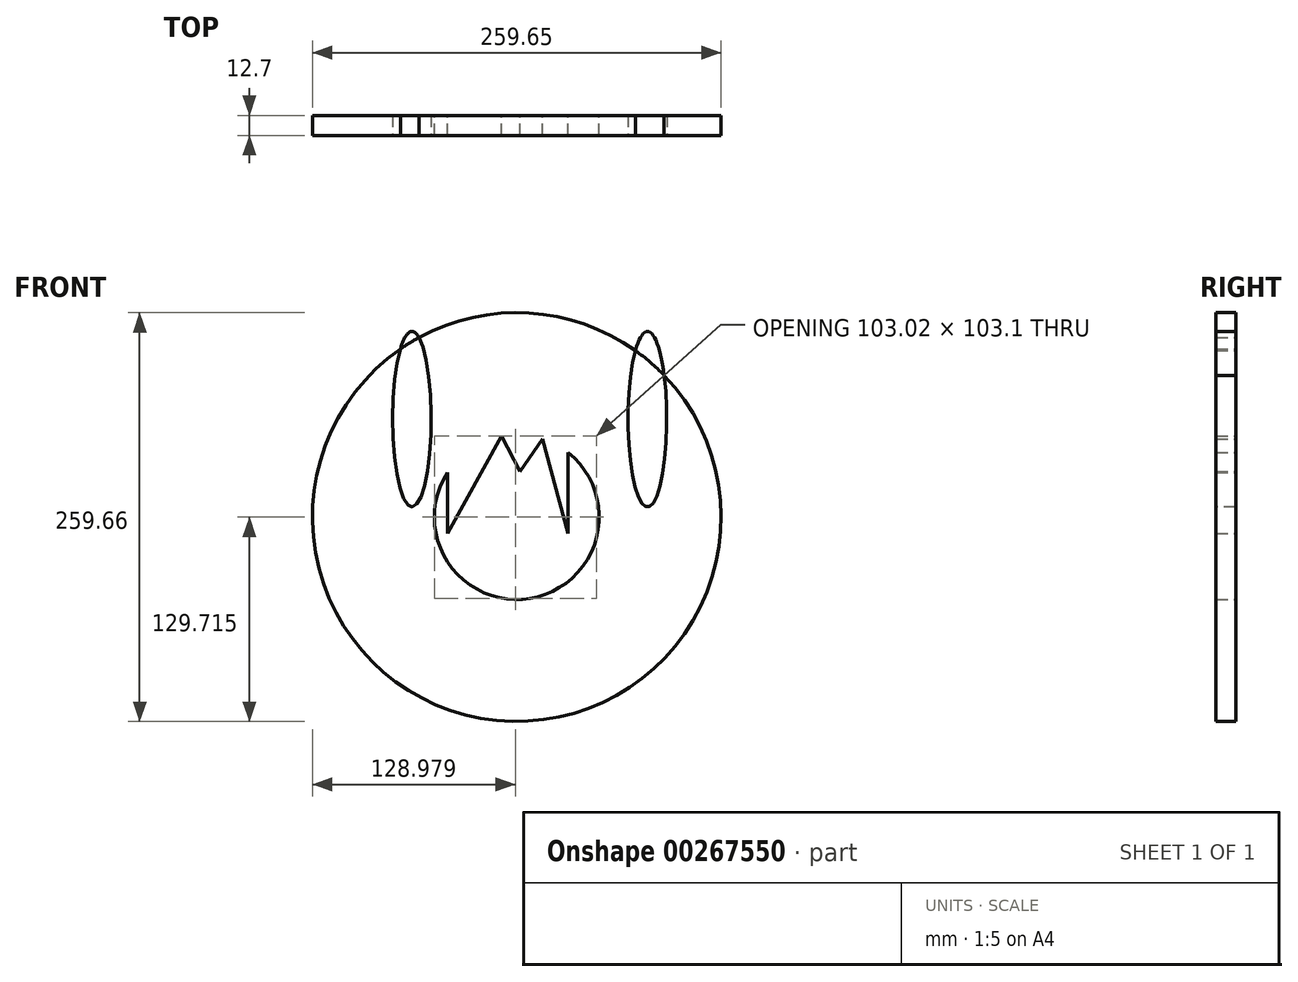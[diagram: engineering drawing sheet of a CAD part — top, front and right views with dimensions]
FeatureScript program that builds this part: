
annotation { "Feature Type Name" : "Feature", "Feature Type Description" : "" }
export const myFeature = defineFeature(function(context is Context, id is Id, definition is map)
    precondition{}
    {
        {
            var Q0;
            Q0=qCreatedBy(makeId("Front.planeOp"),FACE);
            var sketch = newSketch(context, id + "F0", { "sketchPlane" : qUnion([Q0])});
            skCircle(sketch, "E0", {"center": v(-217.67, 116.96) * mm, "radius": 129.83 * mm});
            skEllipse(sketch, "E1", {"center": v(-284.27, 179.1) * mm, "majorRadius": 55.69 * mm, "minorRadius": 12.28 * mm, "majorAxis": v(0, -1)});
            skEllipse(sketch, "E2.MirrorC", {"center": v(-134.69, 179.1) * mm, "majorRadius": 55.69 * mm, "minorRadius": 12.28 * mm, "majorAxis": v(0, -1)});
            skArc(sketch, "E3.0", {"start": v(-261.7, 145.3) * mm, "mid": v(-209.18, 65.3) * mm, "end": v(-185.04, 157.9) * mm});
            skLineSegment(sketch, "E4", {"start": v(-261.7, 145.3) * mm, "end": v(-261.7, 106.38) * mm});
            skLineSegment(sketch, "E5", {"start": v(-261.7, 106.38) * mm, "end": v(-227.46, 168.4) * mm});
            skLineSegment(sketch, "E6", {"start": v(-227.46, 168.4) * mm, "end": v(-215.76, 145.85) * mm});
            skLineSegment(sketch, "E7", {"start": v(-215.76, 145.85) * mm, "end": v(-201.2, 166.65) * mm});
            skLineSegment(sketch, "E8", {"start": v(-201.2, 166.65) * mm, "end": v(-185.04, 106.38) * mm});
            skLineSegment(sketch, "E9", {"start": v(-185.04, 106.38) * mm, "end": v(-185.04, 157.9) * mm});
            skSolve(sketch);
        }
        {
            var Q0;
            {var subQ0=sQuery(id+"F0.wireOp",EDGE,"E2.MirrorC");var subQ1=sQuery(id+"F0.wireOp",EDGE,"E0");var subQ2=makeQuery(id+"F0.imprint","INTERSECT",VERTEX,{"disambiguationData":[OD(0.0)],"derivedFrom":[subQ1,subQ0]});Q0=makeQuery(id+"F0.imprint","IMPRINT",FACE,{"disambiguationData":[TD([[makeQuery(id+"F0.imprint","IMPRINT",EDGE,{"disambiguationData":[TD([[subQ2,1.0]])],"derivedFrom":subQ1}),-1.0]])]});}
            var Q1;
            {var subQ0=sQuery(id+"F0.wireOp",EDGE,"E1");var subQ1=sQuery(id+"F0.wireOp",EDGE,"E0");var subQ2=makeQuery(id+"F0.imprint","INTERSECT",VERTEX,{"disambiguationData":[OD(0.0)],"derivedFrom":[subQ1,subQ0]});Q1=makeQuery(id+"F0.imprint","IMPRINT",FACE,{"disambiguationData":[TD([[makeQuery(id+"F0.imprint","IMPRINT",EDGE,{"disambiguationData":[TD([[subQ2,-1.0]])],"derivedFrom":subQ1}),-1.0]])]});}
            var Q2;
            Q2=makeQuery(id+"F0.imprint","IMPRINT",FACE,{"disambiguationData":[TD([[makeQuery(id+"F0.imprint","IMPRINT",EDGE,{"derivedFrom":sQuery(id+"F0.wireOp",EDGE,"E3.0")}),-1.0]])]});
            extrude(context, id + "F1", {"entities" : qUnion([Q0, Q1, Q2]), "depth" : 12.7 * mm});
        }
    });
